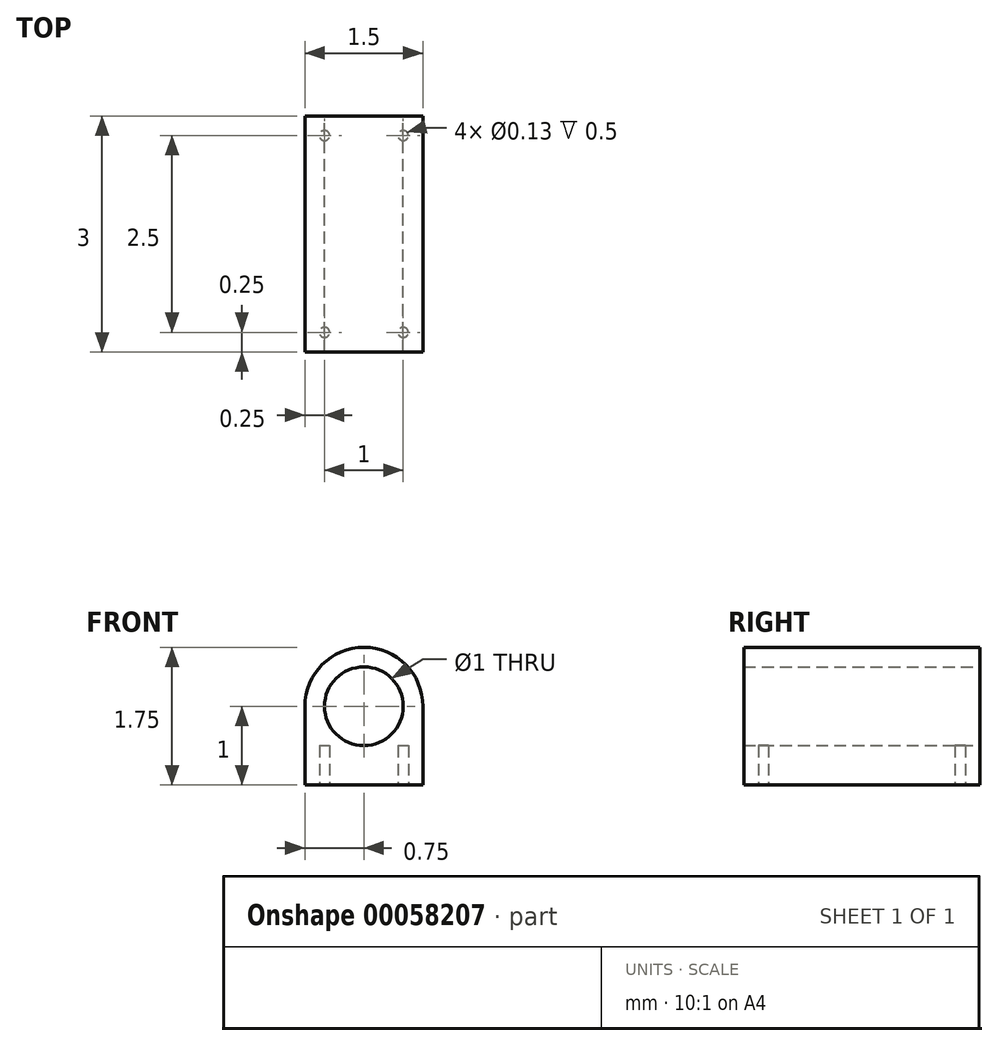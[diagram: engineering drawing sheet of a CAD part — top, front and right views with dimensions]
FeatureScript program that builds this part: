
annotation { "Feature Type Name" : "Feature", "Feature Type Description" : "" }
export const myFeature = defineFeature(function(context is Context, id is Id, definition is map)
    precondition{}
    {
        {
            var Q0;
            Q0=qCreatedBy(makeId("Front.planeOp"),FACE);
            var sketch = newSketch(context, id + "F0", { "sketchPlane" : qUnion([Q0])});
            skLineSegment(sketch, "E0", {"start": v(0, 0) * mm, "end": v(-0.75, 0) * mm});
            skLineSegment(sketch, "E1", {"start": v(-0.75, 0) * mm, "end": v(-0.75, 1) * mm});
            skArc(sketch, "E2", {"start": v(0, 1.75) * mm, "mid": v(-0.53, 1.53) * mm, "end": v(-0.75, 1) * mm});
            skCircle(sketch, "E3", {"center": v(0, 1) * mm, "radius": 0.5 * mm});
            skLineSegment(sketch, "E4.MirrorCS", {"start": v(0.75, 0) * mm, "end": v(0.75, 1) * mm});
            skLineSegment(sketch, "E5.MirrorCS", {"start": v(0, 0) * mm, "end": v(0.75, 0) * mm});
            skArc(sketch, "E6.MirrorCS", {"start": v(0, 1.75) * mm, "mid": v(0.53, 1.53) * mm, "end": v(0.75, 1) * mm});
            skSolve(sketch);
        }
        {
            var Q0;
            Q0=makeQuery(id+"F0.imprint","IMPRINT",FACE,{"disambiguationData":[TD([[makeQuery(id+"F0.imprint","IMPRINT",EDGE,{"derivedFrom":sQuery(id+"F0.wireOp",EDGE,"E0")}),-1.0]])]});
            extrude(context, id + "F1", {"entities" : qUnion([Q0]), "endBound" : BoundingType.SYMMETRIC, "depth" : 3 * mm});
        }
        {
            var Q0;
            Q0=makeQuery(id+"F1.opExtrude","SWEPT_FACE",FACE,{"disambiguationData":[OSD([sQuery(id+"F0.wireOp",EDGE,"E0"),sQuery(id+"F0.wireOp",EDGE,"E5.MirrorCS")])]});
            var sketch = newSketch(context, id + "F2", { "sketchPlane" : qUnion([Q0])});
            skCircle(sketch, "E7", {"center": v(-0.5, 1.25) * mm, "radius": 0.07 * mm});
            skCircle(sketch, "E8.MirrorC", {"center": v(0.5, 1.25) * mm, "radius": 0.07 * mm});
            skCircle(sketch, "E9.MirrorC", {"center": v(0.5, -1.25) * mm, "radius": 0.07 * mm});
            skCircle(sketch, "E10.MirrorC", {"center": v(-0.5, -1.25) * mm, "radius": 0.07 * mm});
            skSolve(sketch);
        }
        {
            var Q0;
            Q0=qSketchRegion(id+"F2",true);
            extrude(context, id + "F3", {"entities" : qUnion([Q0]), "operationType" : NewBodyOperationType.REMOVE, "oppositeDirection" : true, "depth" : 0.5 * mm});
        }
    });
